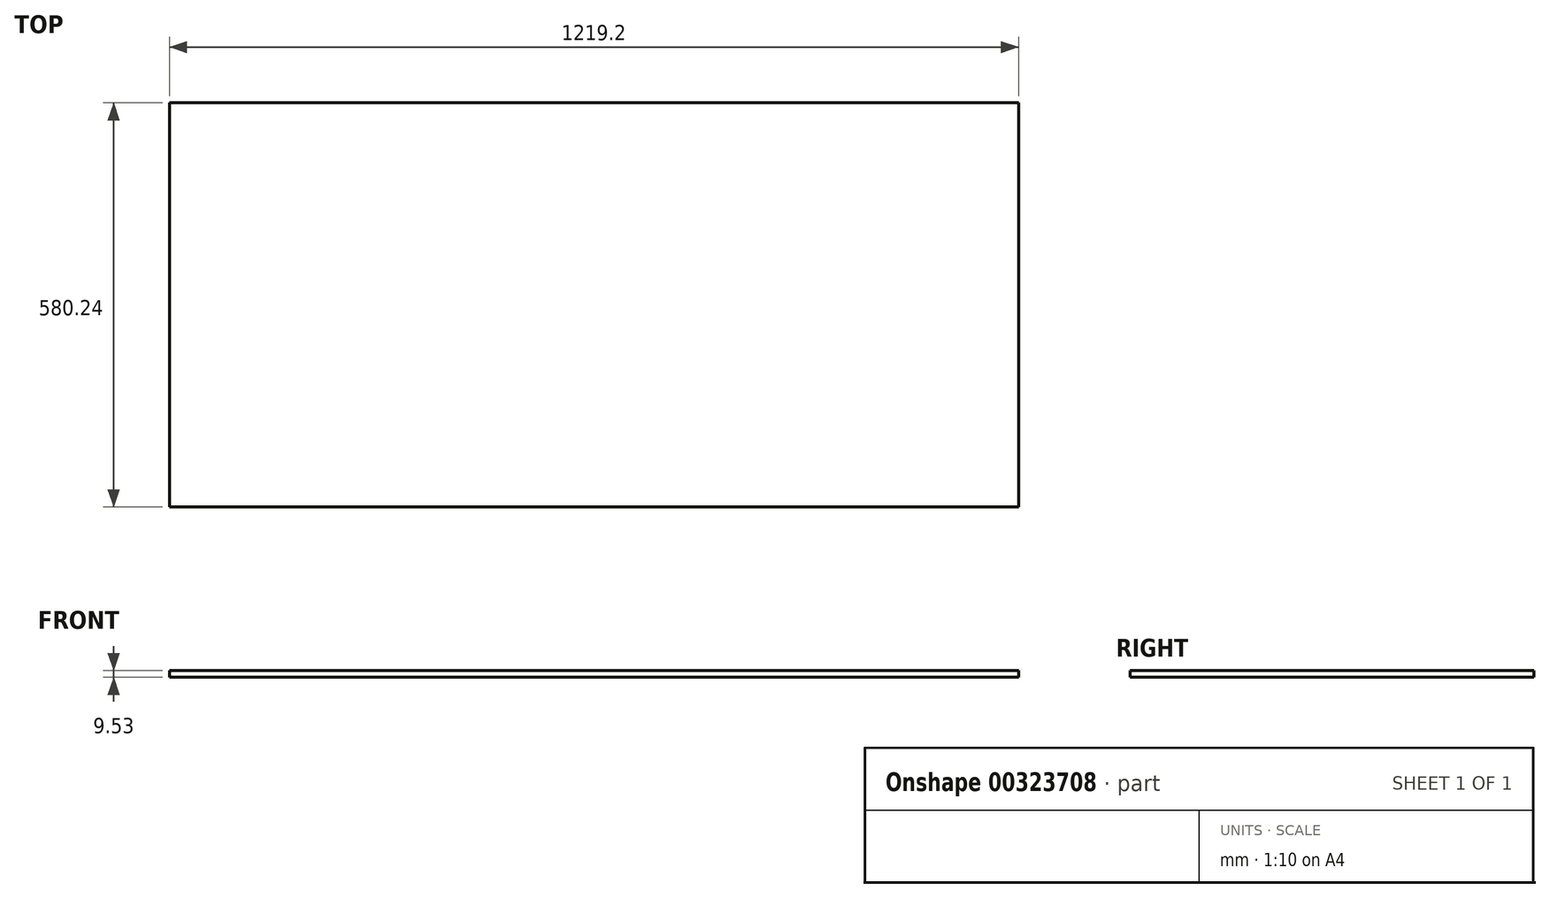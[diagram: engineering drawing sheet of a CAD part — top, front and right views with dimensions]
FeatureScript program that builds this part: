
annotation { "Feature Type Name" : "Feature", "Feature Type Description" : "" }
export const myFeature = defineFeature(function(context is Context, id is Id, definition is map)
    precondition{}
    {
        {
            var Q0;
            Q0=qCreatedBy(makeId("Top.planeOp"),FACE);
            var sketch = newSketch(context, id + "F0", { "sketchPlane" : qUnion([Q0])});
            skLineSegment(sketch, "E0.bottom", {"start": v(609.6, 290.12) * mm, "end": v(-609.6, 290.12) * mm});
            skLineSegment(sketch, "E0.top", {"start": v(609.6, -290.12) * mm, "end": v(-609.6, -290.12) * mm});
            skLineSegment(sketch, "E0.left", {"start": v(609.6, 290.12) * mm, "end": v(609.6, -290.12) * mm});
            skLineSegment(sketch, "E0.right", {"start": v(-609.6, 290.12) * mm, "end": v(-609.6, -290.12) * mm});
            skPoint(sketch, "E0.middle", {"position": v(0, 0) * mm});
            skSolve(sketch);
        }
        {
            var Q0;
            Q0=makeQuery(id+"F0.imprint","IMPRINT",FACE,{"disambiguationData":[TD([[makeQuery(id+"F0.imprint","IMPRINT",EDGE,{"derivedFrom":sQuery(id+"F0.wireOp",EDGE,"E0.bottom")}),1.0]])]});
            extrude(context, id + "F1", {"entities" : qUnion([Q0]), "depth" : 9.52 * mm});
        }
    });
